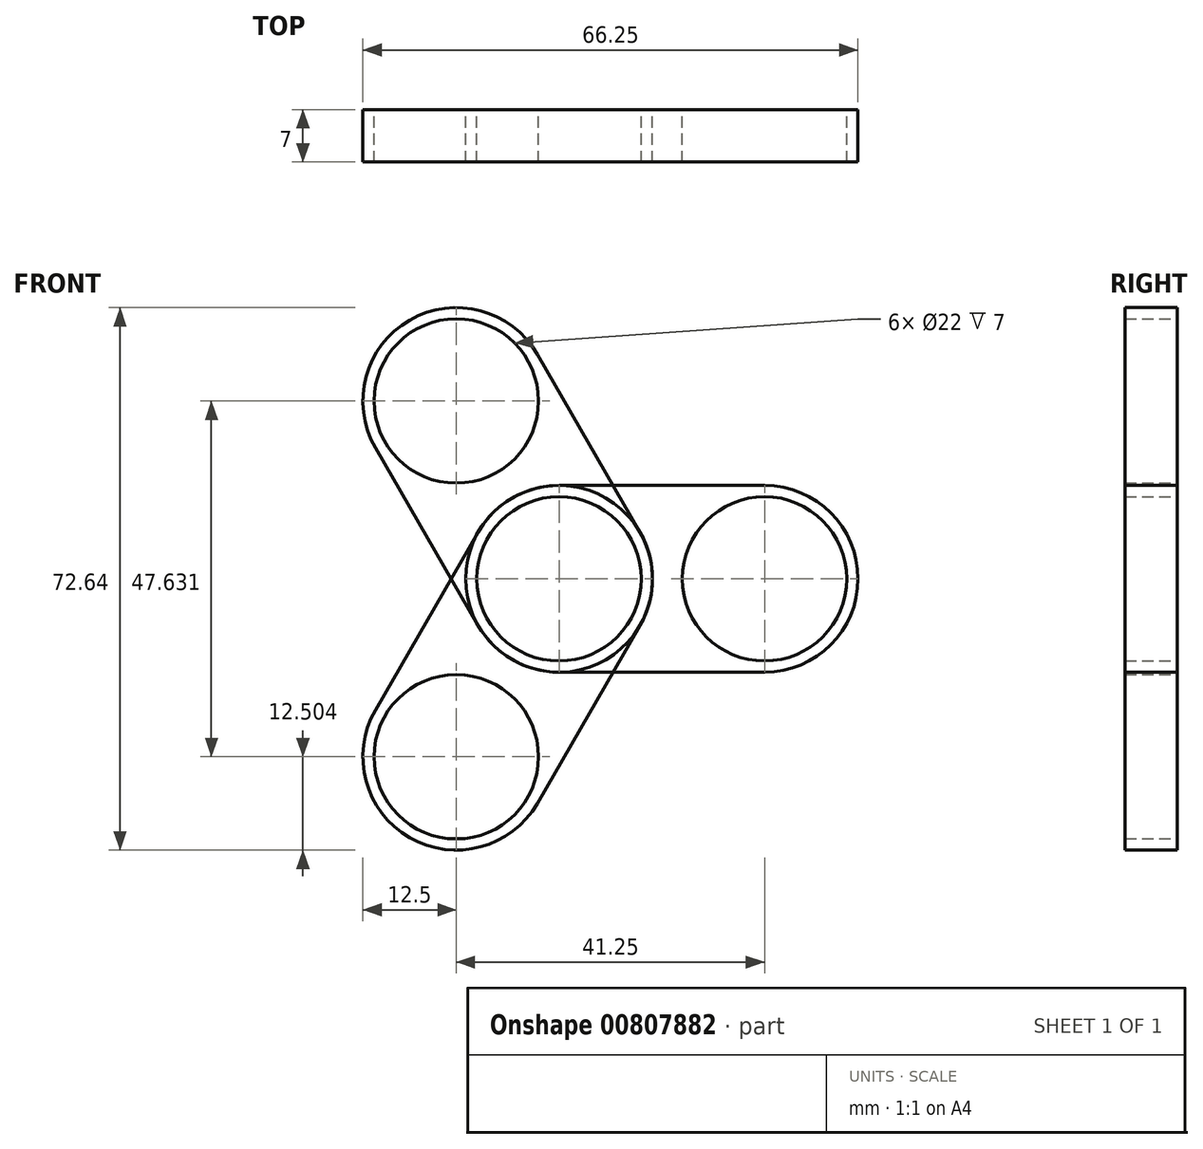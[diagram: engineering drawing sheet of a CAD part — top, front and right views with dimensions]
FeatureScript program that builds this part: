
annotation { "Feature Type Name" : "Feature", "Feature Type Description" : "" }
export const myFeature = defineFeature(function(context is Context, id is Id, definition is map)
    precondition{}
    {
        {
            var Q0;
            Q0=qCreatedBy(makeId("Front.planeOp"),FACE);
            var sketch = newSketch(context, id + "F0", { "sketchPlane" : qUnion([Q0])});
            skCircle(sketch, "E0", {"center": v(0, 0) * mm, "radius": 11 * mm});
            skCircle(sketch, "E1", {"center": v(27.5, 0) * mm, "radius": 12.5 * mm});
            skCircle(sketch, "E2", {"center": v(27.5, 0) * mm, "radius": 11 * mm});
            skCircle(sketch, "E3", {"center": v(0, 0) * mm, "radius": 12.5 * mm});
            skLineSegment(sketch, "E4", {"start": v(0, 12.5) * mm, "end": v(27.5, 12.5) * mm});
            skLineSegment(sketch, "E5", {"start": v(0, -12.5) * mm, "end": v(27.5, -12.5) * mm});
            skSolve(sketch);
        }
        {
            var Q0;
            Q0=makeQuery(id+"F0.imprint","IMPRINT",FACE,{"disambiguationData":[TD([[makeQuery(id+"F0.imprint","IMPRINT",EDGE,{"derivedFrom":sQuery(id+"F0.wireOp",EDGE,"E0")}),-1.0]])]});
            var Q1;
            Q1=makeQuery(id+"F0.imprint","IMPRINT",FACE,{"disambiguationData":[TD([[makeQuery(id+"F0.imprint","IMPRINT",EDGE,{"derivedFrom":sQuery(id+"F0.wireOp",EDGE,"E2")}),-1.0]])]});
            var Q2;
            {var subQ0=sQuery(id+"F0.wireOp",EDGE,"E4");Q2=makeQuery(id+"F0.imprint","IMPRINT",FACE,{"disambiguationData":[TD([[makeQuery(id+"F0.imprint","IMPRINT",EDGE,{"derivedFrom":subQ0}),-1.0]])]});}
            extrude(context, id + "F1", {"entities" : qUnion([Q0, Q1, Q2]), "endBound" : BoundingType.SYMMETRIC, "depth" : 7 * mm, "offsetDistance" : 25 * mm});
        }
        {
            var Q0;
            Q0=qCreatedBy(makeId("Top.planeOp"),FACE);
            var sketch = newSketch(context, id + "F2", { "sketchPlane" : qUnion([Q0])});
            skLineSegment(sketch, "E6", {"start": v(0, 0) * mm, "end": v(0, -42.83) * mm, "construction": true});
            skSolve(sketch);
        }
        {
            var Q0;
            Q0=makeQuery(id+"F1.opExtrude","SWEPT_BODY",BODY,{"disambiguationData":[OSD([sQuery(id+"F0.wireOp",EDGE,"E0"),sQuery(id+"F0.wireOp",EDGE,"E1"),sQuery(id+"F0.wireOp",EDGE,"E2"),sQuery(id+"F0.wireOp",EDGE,"E3"),sQuery(id+"F0.wireOp",EDGE,"E4"),sQuery(id+"F0.wireOp",EDGE,"E5")])]});
            var Q1;
            Q1=sQuery(id+"F2.wireOp",EDGE,"E6");
            circularPattern(context, id + "F3", {"entities" : qUnion([Q0]), "axis" : qUnion([Q1]), "angle" : 360 * degree, "instanceCount" : 3, "equalSpace" : true});
        }
    });
